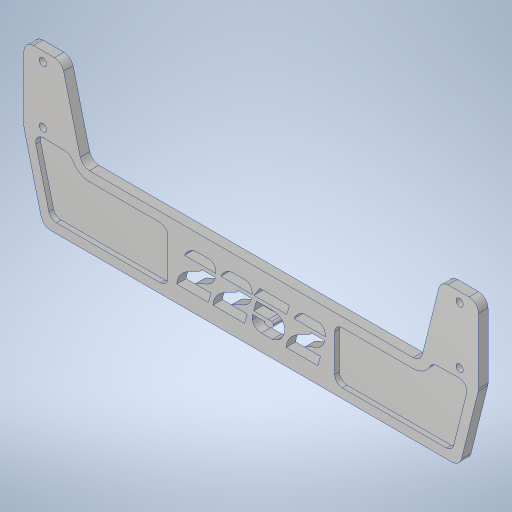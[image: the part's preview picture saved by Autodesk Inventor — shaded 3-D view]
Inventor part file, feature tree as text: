
AUTODESK INVENTOR PART (.ipt)
format: ipt  version: 2023.4 (Build 274418000, 418)  size: 431,104 bytes
history: native  units: in
note: dims shown in document units (in); Inventor stores cm internally (conversion verified against a paired STEP export)
features: sketch x2, extrude x2, fillet x2, hole x1, emboss x1, mirror x1, projected_geometry x1
ambient origin geometry x8: Origin, YZ Plane, XZ Plane, XY Plane, X Axis, Y Axis, Z Axis, Center Point
bodies: Solid1 (feature_tree)
feature tree (10):
  sketch  "Sketch1"  dims[d0=12.0in d1=2.0in]
  extrude  "Extrusion1"  Depth=2.0in
  hole  "Hole1"  [1 undecoded]
  fillet  "Fillet1"  Radius=1.5in
  sketch  "Sketch2"  dims[d2=1.0in d3=1.0in d4=1.5in d5=0.5in d6=0.5in d8=11.0in d9=0.25in d10=0.0in d11=0.201in d12=0.75in d13=0.385in d14=0.25in d15=0.5635in d16=1.0in d17=0.8108in d18=1.875in d19=0.125in d20=0.25in d21=4.0in d22=1.0in d23=3.9in d26=0.25in d27=0.25in d32=0.125in d33=0.0in d34=0.25in d35=0.0in d36=0.2in]
  extrude  "Extrusion2"  Depth=0.5in
  emboss  "Emboss1"
  fillet  "Fillet2"  Radius=0.5in
  mirror  "Mirror1"
  projected_geometry  "Project Cut Edges1"
note: 1 required parameter value undecoded (feature->parameter linkage not recoverable at this tier; creation-order binding heuristic only, values carry confidence <= 0.55)
